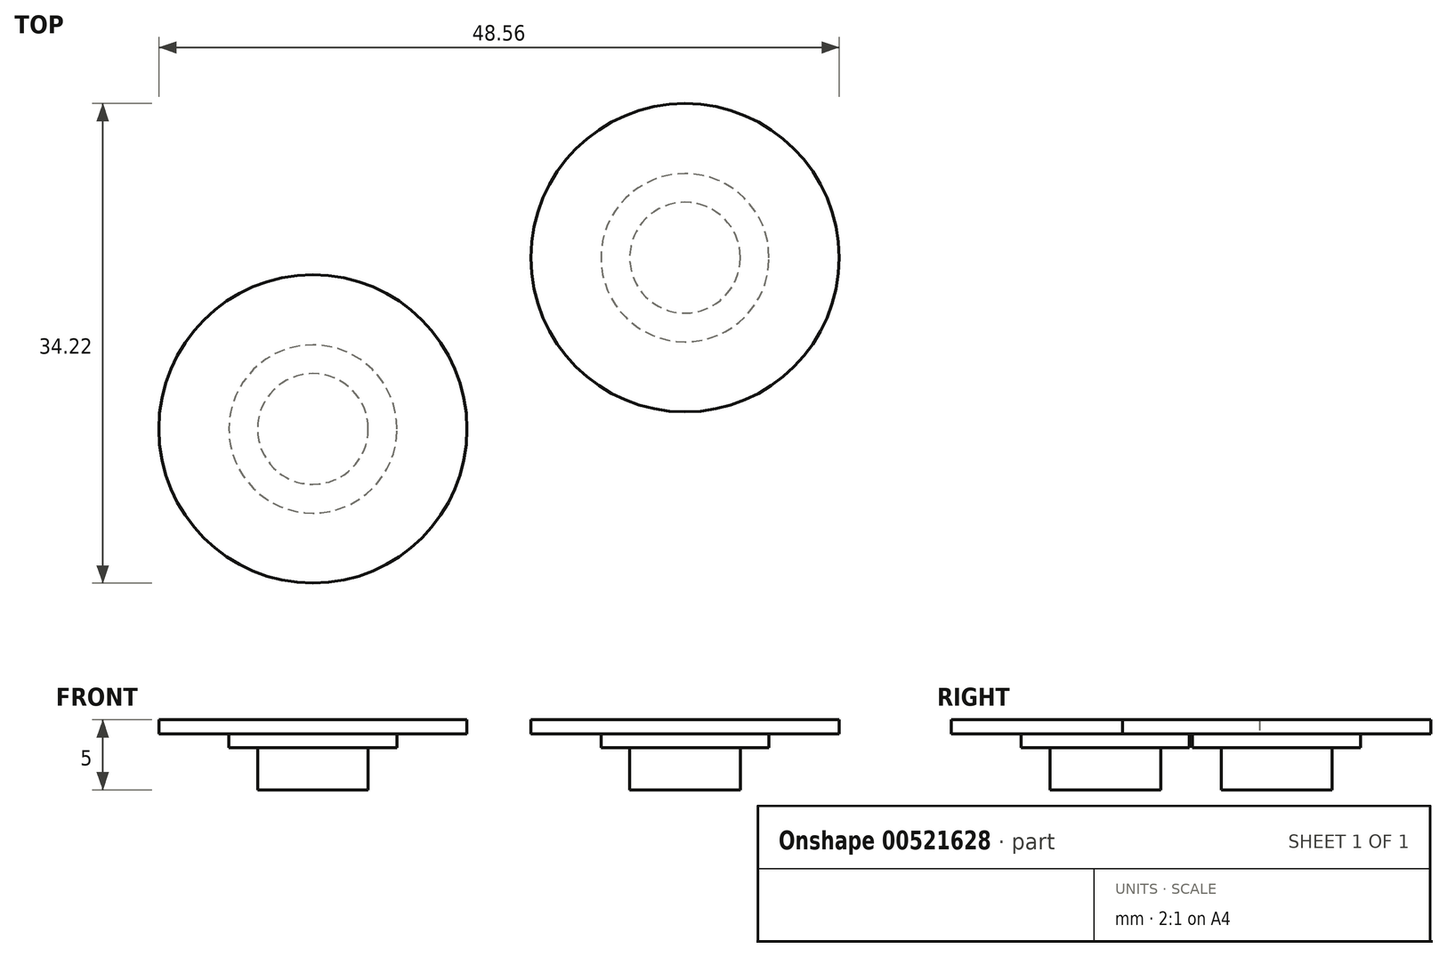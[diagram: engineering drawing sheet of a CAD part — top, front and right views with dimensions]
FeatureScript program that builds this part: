
annotation { "Feature Type Name" : "Feature", "Feature Type Description" : "" }
export const myFeature = defineFeature(function(context is Context, id is Id, definition is map)
    precondition{}
    {
        {
            var Q0;
            Q0=qCreatedBy(makeId("Top.planeOp"),FACE);
            var sketch = newSketch(context, id + "F0", { "sketchPlane" : qUnion([Q0])});
            skCircle(sketch, "E0", {"center": v(-32.58, 7.52) * mm, "radius": 6 * mm});
            skCircle(sketch, "E1", {"center": v(-32.58, 7.52) * mm, "radius": 3.95 * mm});
            skCircle(sketch, "E2", {"center": v(-32.58, 7.52) * mm, "radius": 11 * mm});
            skCircle(sketch, "E3", {"center": v(-6.02, 19.74) * mm, "radius": 6 * mm});
            skCircle(sketch, "E4", {"center": v(-6.02, 19.74) * mm, "radius": 3.95 * mm});
            skCircle(sketch, "E5", {"center": v(-6.02, 19.74) * mm, "radius": 11 * mm});
            skSolve(sketch);
        }
        {
            var Q0;
            Q0=makeQuery(id+"F0.imprint","IMPRINT",FACE,{"disambiguationData":[TD([[makeQuery(id+"F0.imprint","IMPRINT",EDGE,{"derivedFrom":sQuery(id+"F0.wireOp",EDGE,"E0")}),-1.0]])]});
            var Q1;
            Q1=makeQuery(id+"F0.imprint","IMPRINT",FACE,{"disambiguationData":[TD([[makeQuery(id+"F0.imprint","IMPRINT",EDGE,{"derivedFrom":sQuery(id+"F0.wireOp",EDGE,"E0")}),1.0]])]});
            var Q2;
            Q2=makeQuery(id+"F0.imprint","IMPRINT",FACE,{"disambiguationData":[TD([[makeQuery(id+"F0.imprint","IMPRINT",EDGE,{"derivedFrom":sQuery(id+"F0.wireOp",EDGE,"E1")}),1.0]])]});
            var Q3;
            Q3=makeQuery(id+"F0.imprint","IMPRINT",FACE,{"disambiguationData":[TD([[makeQuery(id+"F0.imprint","IMPRINT",EDGE,{"derivedFrom":sQuery(id+"F0.wireOp",EDGE,"E3")}),-1.0]])]});
            var Q4;
            Q4=makeQuery(id+"F0.imprint","IMPRINT",FACE,{"disambiguationData":[TD([[makeQuery(id+"F0.imprint","IMPRINT",EDGE,{"derivedFrom":sQuery(id+"F0.wireOp",EDGE,"E4")}),1.0]])]});
            var Q5;
            Q5=makeQuery(id+"F0.imprint","IMPRINT",FACE,{"disambiguationData":[TD([[makeQuery(id+"F0.imprint","IMPRINT",EDGE,{"derivedFrom":sQuery(id+"F0.wireOp",EDGE,"E3")}),1.0]])]});
            extrude(context, id + "F1", {"entities" : qUnion([Q0, Q1, Q2, Q3, Q4, Q5]), "depth" : 1 * mm, "offsetDistance" : 25 * mm});
        }
        {
            var Q0;
            Q0=makeQuery(id+"F0.imprint","IMPRINT",FACE,{"disambiguationData":[TD([[makeQuery(id+"F0.imprint","IMPRINT",EDGE,{"derivedFrom":sQuery(id+"F0.wireOp",EDGE,"E1")}),1.0]])]});
            var Q1;
            Q1=makeQuery(id+"F0.imprint","IMPRINT",FACE,{"disambiguationData":[TD([[makeQuery(id+"F0.imprint","IMPRINT",EDGE,{"derivedFrom":sQuery(id+"F0.wireOp",EDGE,"E4")}),1.0]])]});
            extrude(context, id + "F2", {"entities" : qUnion([Q0, Q1]), "operationType" : NewBodyOperationType.ADD, "oppositeDirection" : true, "depth" : 4 * mm, "offsetDistance" : 25 * mm});
        }
        {
            var Q0;
            Q0=makeQuery(id+"F0.imprint","IMPRINT",FACE,{"disambiguationData":[TD([[makeQuery(id+"F0.imprint","IMPRINT",EDGE,{"derivedFrom":sQuery(id+"F0.wireOp",EDGE,"E0")}),1.0]])]});
            var Q1;
            Q1=makeQuery(id+"F0.imprint","IMPRINT",FACE,{"disambiguationData":[TD([[makeQuery(id+"F0.imprint","IMPRINT",EDGE,{"derivedFrom":sQuery(id+"F0.wireOp",EDGE,"E3")}),1.0]])]});
            extrude(context, id + "F3", {"entities" : qUnion([Q0, Q1]), "operationType" : NewBodyOperationType.ADD, "oppositeDirection" : true, "depth" : 1 * mm, "offsetDistance" : 25 * mm});
        }
    });
